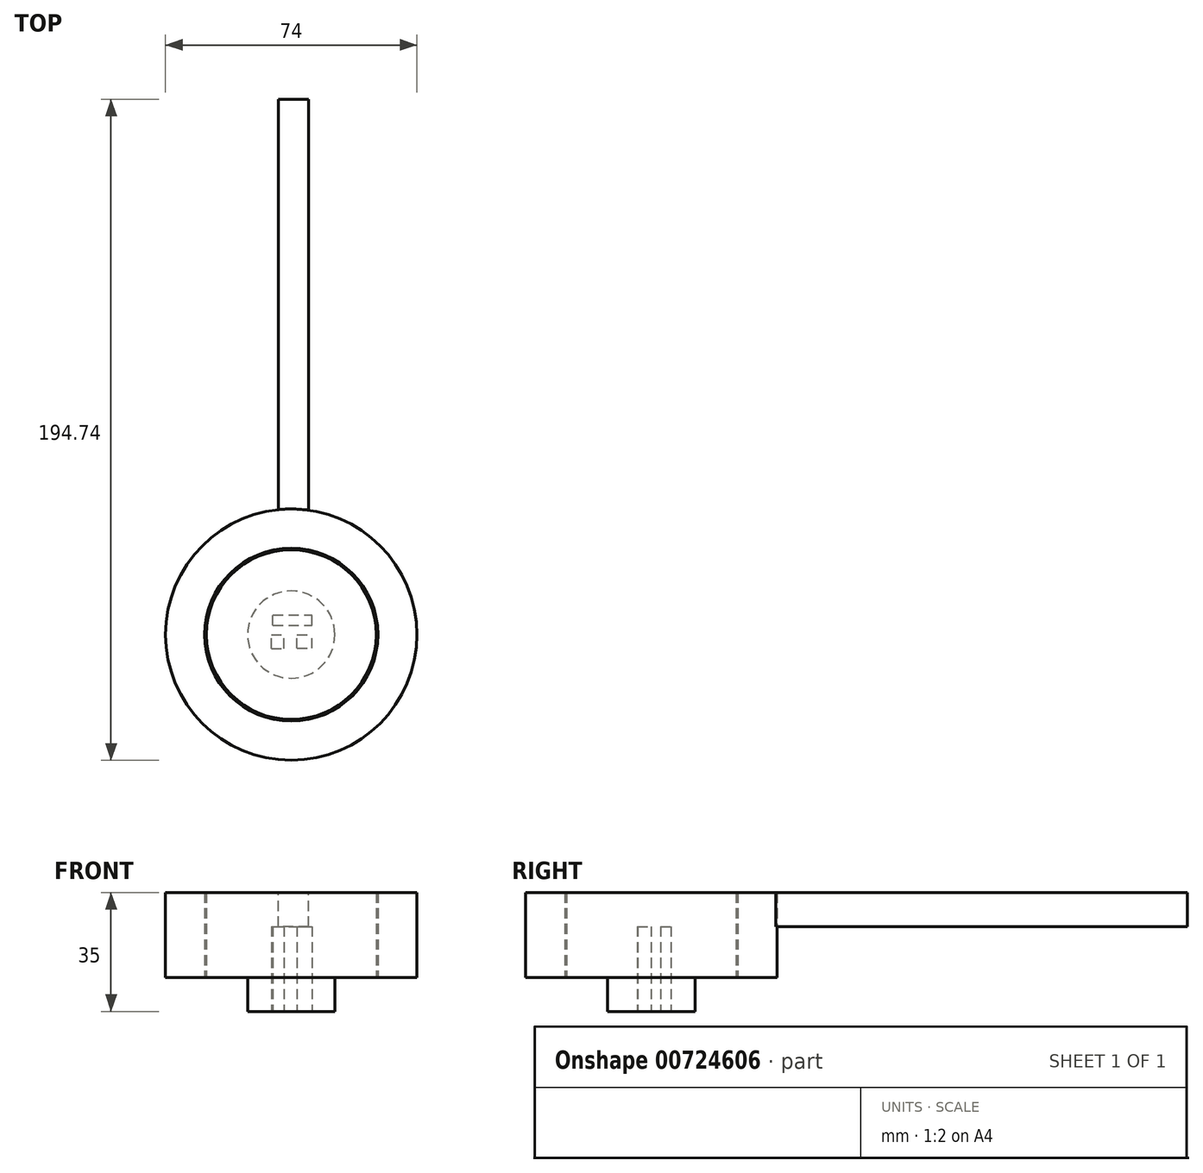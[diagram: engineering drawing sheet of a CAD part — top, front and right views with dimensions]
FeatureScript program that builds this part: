
annotation { "Feature Type Name" : "Feature", "Feature Type Description" : "" }
export const myFeature = defineFeature(function(context is Context, id is Id, definition is map)
    precondition{}
    {
        {
            var Q0;
            Q0=qCreatedBy(makeId("Top.planeOp"),FACE);
            var sketch = newSketch(context, id + "F0", { "sketchPlane" : qUnion([Q0])});
            skCircle(sketch, "E0", {"center": v(0, 0) * mm, "radius": 25 * mm});
            skCircle(sketch, "E1.0", {"center": v(0, 0) * mm, "radius": 37 * mm});
            skCircle(sketch, "E2.0", {"center": v(0, 0) * mm, "radius": 25.5 * mm});
            skSolve(sketch);
        }
        {
            var Q0;
            Q0=makeQuery(id+"F0.imprint","IMPRINT",FACE,{"disambiguationData":[TD([[makeQuery(id+"F0.imprint","IMPRINT",EDGE,{"derivedFrom":sQuery(id+"F0.wireOp",EDGE,"E0")}),1.0]])]});
            extrude(context, id + "F1", {"entities" : qUnion([Q0]), "depth" : 25 * mm, "offsetDistance" : 25 * mm});
        }
        {
            var Q0;
            Q0=makeQuery(id+"F0.imprint","IMPRINT",FACE,{"disambiguationData":[TD([[makeQuery(id+"F0.imprint","IMPRINT",EDGE,{"derivedFrom":sQuery(id+"F0.wireOp",EDGE,"E1.0")}),1.0]])]});
            extrude(context, id + "F2", {"entities" : qUnion([Q0]), "depth" : 25 * mm, "offsetDistance" : 25 * mm});
        }
        {
            var Q0;
            Q0=makeQuery(id+"F2.opExtrude","CAP_FACE",FACE,{"disambiguationData":[OSD([sQuery(id+"F0.wireOp",EDGE,"E1.0"),sQuery(id+"F0.wireOp",EDGE,"E2.0")])],"isStart":false});
            var sketch = newSketch(context, id + "F3", { "sketchPlane" : qUnion([Q0])});
            skLineSegment(sketch, "E3", {"start": v(5.16, 36.64) * mm, "end": v(5.16, 109.24) * mm});
            skLineSegment(sketch, "E4", {"start": v(5.16, 109.24) * mm, "end": v(-3.82, 109.24) * mm});
            skLineSegment(sketch, "E5", {"start": v(-3.82, 109.24) * mm, "end": v(-3.82, 36.8) * mm});
            skLineSegment(sketch, "E6", {"start": v(-3.82, 36.8) * mm, "end": v(5.16, 36.64) * mm});
            skSolve(sketch);
        }
        {
            var Q0;
            {var subQ0=sQuery(id+"F3.wireOp",EDGE,"E3");Q0=makeQuery(id+"F3.imprint","IMPRINT",FACE,{"disambiguationData":[TD([[makeQuery(id+"F3.imprint","IMPRINT",EDGE,{"derivedFrom":subQ0}),1.0]])]});}
            extrude(context, id + "F4", {"entities" : qUnion([Q0]), "oppositeDirection" : true, "depth" : 10 * mm, "offsetDistance" : 25 * mm});
        }
        {
            var Q0;
            Q0=makeQuery(id+"F4.opExtrude","SWEPT_FACE",FACE,{"disambiguationData":[OSD([sQuery(id+"F3.wireOp",EDGE,"E4")])]});
            extrude(context, id + "F5", {"entities" : qUnion([Q0]), "operationType" : NewBodyOperationType.ADD, "depth" : 48.5 * mm, "offsetDistance" : 25 * mm});
        }
        {
            var Q0;
            Q0=makeQuery(id+"F1.opExtrude","CAP_FACE",FACE,{"disambiguationData":[OSD([sQuery(id+"F0.wireOp",EDGE,"E0")])],"isStart":true});
            var sketch = newSketch(context, id + "F6", { "sketchPlane" : qUnion([Q0])});
            skCircle(sketch, "E7", {"center": v(0, 0) * mm, "radius": 12.85 * mm});
            skSolve(sketch);
        }
        {
            var Q0;
            Q0=makeQuery(id+"F6.imprint","IMPRINT",FACE,{"disambiguationData":[TD([[makeQuery(id+"F6.imprint","IMPRINT",EDGE,{"derivedFrom":sQuery(id+"F6.wireOp",EDGE,"E7")}),1.0]])]});
            extrude(context, id + "F7", {"entities" : qUnion([Q0]), "operationType" : NewBodyOperationType.ADD, "depth" : 10 * mm, "offsetDistance" : 25 * mm});
        }
        {
            var Q0;
            Q0=makeQuery(id+"F7.opExtrude","CAP_FACE",FACE,{"disambiguationData":[OSD([sQuery(id+"F6.wireOp",EDGE,"E7")])],"isStart":false});
            var sketch = newSketch(context, id + "F8", { "sketchPlane" : qUnion([Q0])});
            skLineSegment(sketch, "E8.bottom", {"start": v(-5.87, 4.12) * mm, "end": v(-2.13, 4.12) * mm});
            skLineSegment(sketch, "E8.top", {"start": v(-5.87, 0) * mm, "end": v(-2.13, 0) * mm});
            skLineSegment(sketch, "E8.left", {"start": v(-5.87, 4.12) * mm, "end": v(-5.87, 0) * mm});
            skLineSegment(sketch, "E8.right", {"start": v(-2.13, 4.12) * mm, "end": v(-2.13, 0) * mm});
            skLineSegment(sketch, "E9.bottom", {"start": v(1.7, 4.03) * mm, "end": v(6.17, 4.03) * mm});
            skLineSegment(sketch, "E9.top", {"start": v(1.7, 0) * mm, "end": v(6.17, 0) * mm});
            skLineSegment(sketch, "E9.left", {"start": v(1.7, 4.03) * mm, "end": v(1.7, 0) * mm});
            skLineSegment(sketch, "E9.right", {"start": v(6.17, 4.03) * mm, "end": v(6.17, 0) * mm});
            skLineSegment(sketch, "E10.bottom", {"start": v(-5.4, -2.7) * mm, "end": v(6.17, -2.7) * mm});
            skLineSegment(sketch, "E10.top", {"start": v(-5.4, -5.77) * mm, "end": v(6.17, -5.77) * mm});
            skLineSegment(sketch, "E10.left", {"start": v(-5.4, -2.7) * mm, "end": v(-5.4, -5.77) * mm});
            skLineSegment(sketch, "E10.right", {"start": v(6.17, -2.7) * mm, "end": v(6.17, -5.77) * mm});
            skSolve(sketch);
        }
        {
            var Q0;
            Q0=makeQuery(id+"F8.imprint","IMPRINT",FACE,{"disambiguationData":[TD([[makeQuery(id+"F8.imprint","IMPRINT",EDGE,{"derivedFrom":sQuery(id+"F8.wireOp",EDGE,"E8.bottom")}),-1.0]])]});
            var Q1;
            Q1=makeQuery(id+"F8.imprint","IMPRINT",FACE,{"disambiguationData":[TD([[makeQuery(id+"F8.imprint","IMPRINT",EDGE,{"derivedFrom":sQuery(id+"F8.wireOp",EDGE,"E9.bottom")}),-1.0]])]});
            var Q2;
            Q2=makeQuery(id+"F8.imprint","IMPRINT",FACE,{"disambiguationData":[TD([[makeQuery(id+"F8.imprint","IMPRINT",EDGE,{"derivedFrom":sQuery(id+"F8.wireOp",EDGE,"E10.bottom")}),-1.0]])]});
            extrude(context, id + "F9", {"entities" : qUnion([Q0, Q1, Q2]), "operationType" : NewBodyOperationType.REMOVE, "oppositeDirection" : true, "depth" : 25 * mm, "offsetDistance" : 25 * mm});
        }
    });
